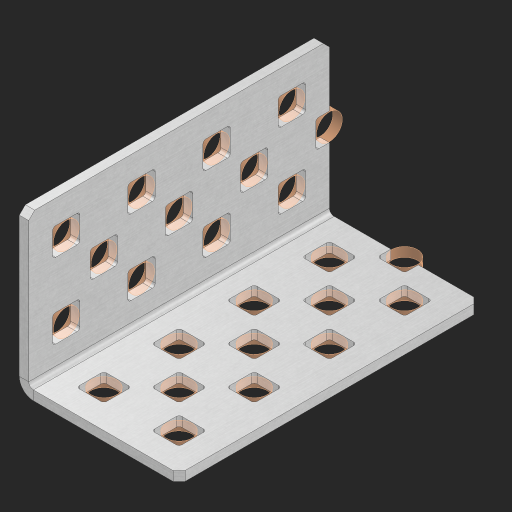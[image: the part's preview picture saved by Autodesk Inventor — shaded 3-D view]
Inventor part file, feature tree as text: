
AUTODESK INVENTOR PART (.ipt)
format: ipt  version: 2023 (Build 270158000, 158)  size: 684,544 bytes
history: native  units: in
note: dims shown in document units (in); Inventor stores cm internally (conversion verified against a paired STEP export)
features: other x30, extrude x22, sheet_metal_op x8, sketch x7, pattern_linear x2, mirror x1, chamfer x1
ambient origin geometry x8: Origin, YZ Plane, XZ Plane, XY Plane, X Axis, Y Axis, Z Axis, Center Point
bodies: Solid1 (feature_tree), Body (feature_tree)
feature tree (71):
  sheet_metal_op  "Flanges"
  sheet_metal_op  "Body Pattern"
  pattern_linear  "Center Pattern"  Spacing1=1.0in  [1 undecoded]
  other  "Arc Length"
  pattern_linear  "Notch Pattern"  Spacing1=0.25in  [1 undecoded]
  other  "Diagonal Plane"
  mirror  "Everything Mirrored"
  chamfer  "End Chamfer"
  sketch  "Sketch1"  dims[d0=1.0in]
  other  "Plate1"
  sketch  "Sketch2"  dims[d1=2.0in]
  other  "Plate2"
  sheet_metal_op  "Bend1"
  sheet_metal_op  "Corner1"
  sketch  "Sketch8"  dims[d2=0.0625in]
  sketch  "Sketch9"  dims[d3=0.0625in]
  other  "Srf91"
  sheet_metal_op  "Body Pattern Sketch"
  other  "Srf92"
  sketch  "Sketch13"  dims[d4=0.0312in]
  sketch  "Sketch15"  dims[d5=0.125in]
  sketch  "Sketch16"  dims[d6=0.0625in d7=1.0in d8=90.0deg d9=0.0312in d10=0.25in d11=0.0625in d12=0.0625in d49=0.182in d50=0.02in d52=0.25in d53=0.0625in d54=0.0in d55=0.172in d56=1.0in d57=0.0in d60=1.5748in d62=0.5in d63=0.7874in d65=0.5in d85=0.1473in d86=0.1782in d89=0.0625in d90=0.0in d91=0.04in d92=0.0491in d95=2.5in d96=0.04in d97=0.25in d98=45.0deg d99=0.25in d106=0.182in d107=0.02in d108=0.5in d110=0.0625in d111=0.0in d112=0.172in d113=0.5in d114=0.0in d117=0.5in d123=0.25in d125=0.25in d126=0.0491in d127=0.1473in d128=0.08in d129=0.04in d130=2.5in]
  other  "Srf786"
  other  "Srf856"
  other  "Srf857"
  other  "Srf858"
  other  "Srf859"
  other  "Srf860"
  other  "Srf861"
  other  "Srf889"
  other  "Srf890"
  other  "Srf891"
  other  "Srf1275"
  other  "Srf1276"
  other  "Srf1278"
  other  "Srf1279"
  other  "Srf1280"
  other  "Srf1281"
  other  "Srf1282"
  other  "Srf1283"
  other  "Srf1277"
  other  "Srf1285"
  other  "Srf1286"
  other  "Srf1287"
  sheet_metal_op  "Body Stamp"
  sheet_metal_op  "Body Circle"
  other  "Center Stamp"
  other  "Center Circle"
  sheet_metal_op  "Notch"
  extrude  "ExtrusionSrf92"  Depth=0.0625in
  extrude  "ExtrusionSrf856"  Depth=0.0625in
  extrude  "ExtrusionSrf857"  Depth=0.182in
  extrude  "ExtrusionSrf858"  Depth=0.02in
  extrude  "ExtrusionSrf859"  Depth=0.25in
  extrude  "ExtrusionSrf860"  Depth=0.0625in
  extrude  "ExtrusionSrf861"  TaperAngle=0.0deg  [1 undecoded]
  extrude  "ExtrusionSrf889"  Depth=0.25in
  extrude  "ExtrusionSrf890"  Depth=1.0in TaperAngle=0.0deg
  extrude  "ExtrusionSrf891"  Depth=0.25in
  extrude  "ExtrusionSrf1275"  Depth=0.5in
  extrude  "ExtrusionSrf1276"  Depth=0.25in
  extrude  "ExtrusionSrf1277"  Depth=0.25in
  extrude  "ExtrusionSrf1278"  Depth=0.0625in
  extrude  "ExtrusionSrf1279"  Depth=0.25in TaperAngle=0.0deg
  extrude  "ExtrusionSrf1280"  Depth=0.25in
  extrude  "ExtrusionSrf1281"  Depth=0.25in TaperAngle=45.0deg
  extrude  "ExtrusionSrf1282"  Depth=0.25in
  extrude  "ExtrusionSrf1345"  Depth=0.182in
  extrude  "ExtrusionSrf1346"  Depth=0.02in
  extrude  "ExtrusionSrf1347"  Depth=0.5in
  extrude  "ExtrusionSrf1348"  Depth=0.0625in
note: 3 required parameter values undecoded (feature->parameter linkage not recoverable at this tier; creation-order binding heuristic only, values carry confidence <= 0.55)
